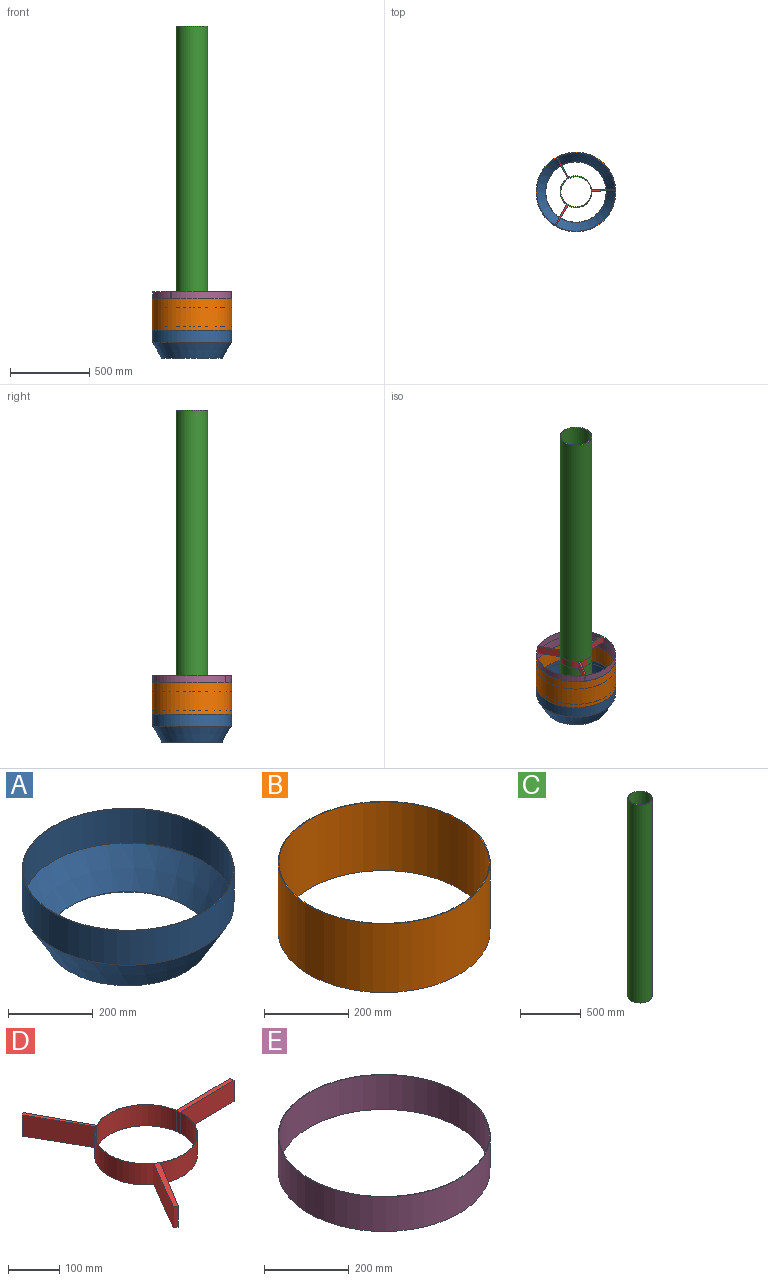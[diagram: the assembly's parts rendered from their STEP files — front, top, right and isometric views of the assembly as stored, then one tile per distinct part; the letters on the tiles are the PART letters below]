
ASSEMBLY  parts=5 mates=6
PART A: 6 faces, bbox 500x500x200 mm
  f0: cylinder r=250mm len=500mm, axis (0,0,-1), area 157079.6mm2, adj f1,f2
  f1: plane 500x500mm, normal (0,0,1), area 2349.1mm2, adj f0,f4
  f2: cone r=250mm half-angle=30deg, axis (0,0,1), area 160436mm2, adj f0,f3
  f3: plane 384.53x384.53mm, normal (0,0,-1), area 2083mm2, adj f2,f5
  f4: cylinder r=248.5mm len=497mm, axis (0,0,-1), area 155509.6mm2, adj f1,f5
  f5: cone r=248.7mm half-angle=30deg, axis (0,0,1), area 159903.6mm2, adj f3,f4
PART B: 4 faces, bbox 504x504x200 mm
  f0: cylinder r=252mm len=504mm, axis (0,0,-1), area 316672.5mm2, adj f1,f2
  f1: plane 504x504mm, normal (0,0,1), area 3154.2mm2, adj f0,f3
  f2: plane 504x504mm, normal (0,0,-1), area 3154.2mm2, adj f0,f3
  f3: cylinder r=250mm len=500mm, axis (0,0,-1), area 314159.3mm2, adj f1,f2
PART C: 4 faces, bbox 200x200x2000 mm
  f0: cylinder r=96mm len=2000mm, axis (0,0,-1), area 1206371.6mm2, adj f2,f3
  f1: cylinder r=100mm len=2000mm, axis (0,0,-1), area 1256637.1mm2, adj f2,f3
  f2: plane 200x200mm, normal (0,0,1), area 2463mm2, adj f0,f1
  f3: plane 200x200mm, normal (0,0,-1), area 2463mm2, adj f0,f1
PART D: 15 faces, bbox 383.5x434.8x50 mm
  f0: plane 129.75x73.77mm, normal (-0.87,-0.49,0), area 7462.9mm2, adj f1,f11,f13,f14
  f1: cylinder r=100mm len=166.68mm, axis (0,0,-1), area 9872.6mm2, adj f0,f2,f13,f14
  f2: plane 129.41x75.07mm, normal (-0.86,0.5,0), area 7480.4mm2, adj f1,f3,f13,f14
  f3: plane 50x7.76mm, normal (-0.52,-0.85,0), area 455.3mm2, adj f2,f4,f13,f14
  f4: plane 127.23x78.15mm, normal (0.85,-0.52,0), area 7465.5mm2, adj f3,f5,f13,f14
  f5: cylinder r=100mm len=148.47mm, axis (0,0,-1), area 10651.2mm2, adj f4,f6,f13,f14
  f6: plane 149.29x50mm, normal (0.01,-1,0), area 7465mm2, adj f5,f7,f13,f14
  f7: plane 50x9.93mm, normal (1,0.05,0), area 497.2mm2, adj f6,f8,f13,f14
  f8: plane 149.84x50mm, normal (-0.01,1,0), area 7492.7mm2, adj f7,f9,f13,f14
  f9: cylinder r=100mm len=145.08mm, axis (0,0,-1), area 9487.8mm2, adj f8,f10,f13,f14
  f10: plane 131.46x70.68mm, normal (0.88,0.47,0), area 7462.7mm2, adj f9,f11,f13,f14
  f11: plane 50x7.56mm, normal (-0.48,0.87,0), area 432.2mm2, adj f0,f10,f13,f14
  f12: cylinder r=99.25mm len=198.5mm, axis (0,0,-1), area 31180.3mm2, adj f13,f14
  f13: plane 434.8x383.52mm, normal (0,0,1), area 4629.6mm2, adj f0,f1,f2,f3,f4,f5,f6,f7
  f14: plane 434.8x383.52mm, normal (0,0,-1), area 4629.6mm2, adj f0,f1,f2,f3,f4,f5,f6,f7
PART E: 4 faces, bbox 500x500x100 mm
  f0: cylinder r=250mm len=500mm, axis (0,0,-1), area 157079.6mm2, adj f1,f2
  f1: plane 500x500mm, normal (0,0,1), area 2349.1mm2, adj f0,f3
  f2: plane 500x500mm, normal (0,0,-1), area 2349.1mm2, adj f0,f3
  f3: cylinder r=248.5mm len=497mm, axis (0,0,-1), area 156137.2mm2, adj f1,f2
PLACE A t=(-134.29,-1386.5,671.92)mm
PLACE B rot(axis=(1,0,0),180deg) t=(-134.29,-1386.5,946.92)mm
PLACE C t=(-134.29,-1386.5,671.92)mm
PLACE D t=(-105.19,-1400.53,945.57)mm
PLACE E t=(-134.29,-1386.5,889.97)mm
MATE planar C.f1 <-> A.f0  axis (0,0,-1) through (-134.29,-1386.5,671.92)mm
MATE cylindrical D.f1 <-> C.f1  axis (0,0,1) through (-134.29,-1386.5,995.57)mm
MATE fastened B.f0 <-> A.f0  axis (0,0,1) through (-134.29,-1386.5,946.92)mm
MATE cylindrical B.f0 <-> C.f1  axis (0,0,1) through (-134.29,-1386.5,846.92)mm
MATE cylindrical C.f1 <-> E.f0  axis (0,0,-1) through (-134.29,-1386.5,1671.92)mm
MATE cylindrical A.f0 <-> C.f1  axis (0,0,-1) through (-134.29,-1386.5,722.12)mm
